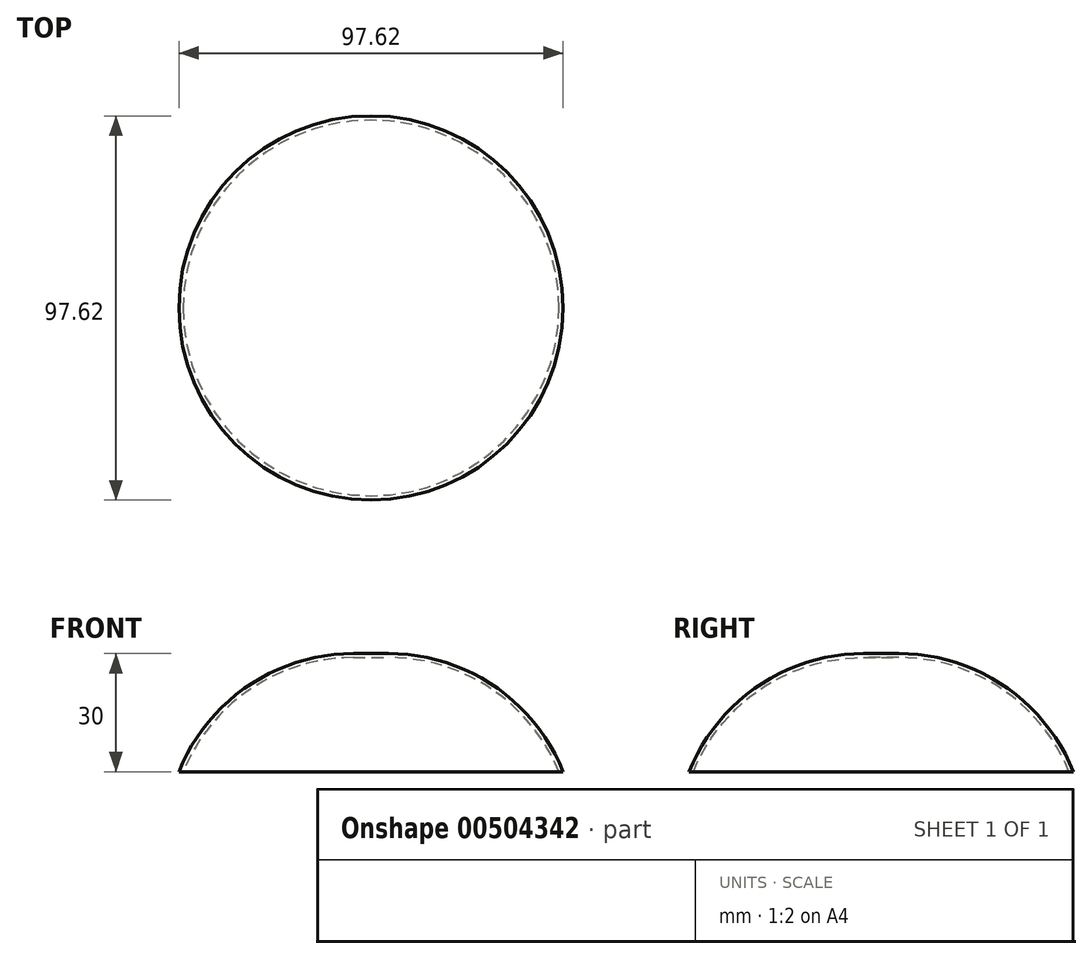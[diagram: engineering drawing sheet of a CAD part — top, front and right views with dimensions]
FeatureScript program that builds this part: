
annotation { "Feature Type Name" : "Feature", "Feature Type Description" : "" }
export const myFeature = defineFeature(function(context is Context, id is Id, definition is map)
    precondition{}
    {
        {
            var Q0;
            Q0=qCreatedBy(makeId("Top.planeOp"),FACE);
            var sketch = newSketch(context, id + "F0", { "sketchPlane" : qUnion([Q0])});
            skCircle(sketch, "E0", {"center": v(0, 0) * mm, "radius": 48.81 * mm});
            skSolve(sketch);
        }
        {
            var Q0;
            Q0=makeQuery(id+"F0.imprint","IMPRINT",FACE,{"disambiguationData":[TD([[makeQuery(id+"F0.imprint","IMPRINT",EDGE,{"derivedFrom":sQuery(id+"F0.wireOp",EDGE,"E0")}),1.0]])]});
            extrude(context, id + "F1", {"entities" : qUnion([Q0]), "depth" : 30 * mm, "offsetDistance" : 25 * mm});
        }
        {
            var Q0;
            Q0=makeQuery(id+"F1.opExtrude","CAP_FACE",FACE,{"disambiguationData":[OSD([sQuery(id+"F0.wireOp",EDGE,"E0")])],"isStart":false});
            fillet(context, id + "F2", {"entities" : qUnion([Q0]), "radius" : 47.8 * mm, "tangentPropagation" : true, "allowEdgeOverflow" : false});
        }
        {
            var Q0;
            Q0=makeQuery(id+"F1.opExtrude","CAP_FACE",FACE,{"disambiguationData":[OSD([sQuery(id+"F0.wireOp",EDGE,"E0")])],"isStart":true});
            shell(context, id + "F3", {"entities" : qUnion([Q0]), "thickness" : 1 * mm});
        }
    });
